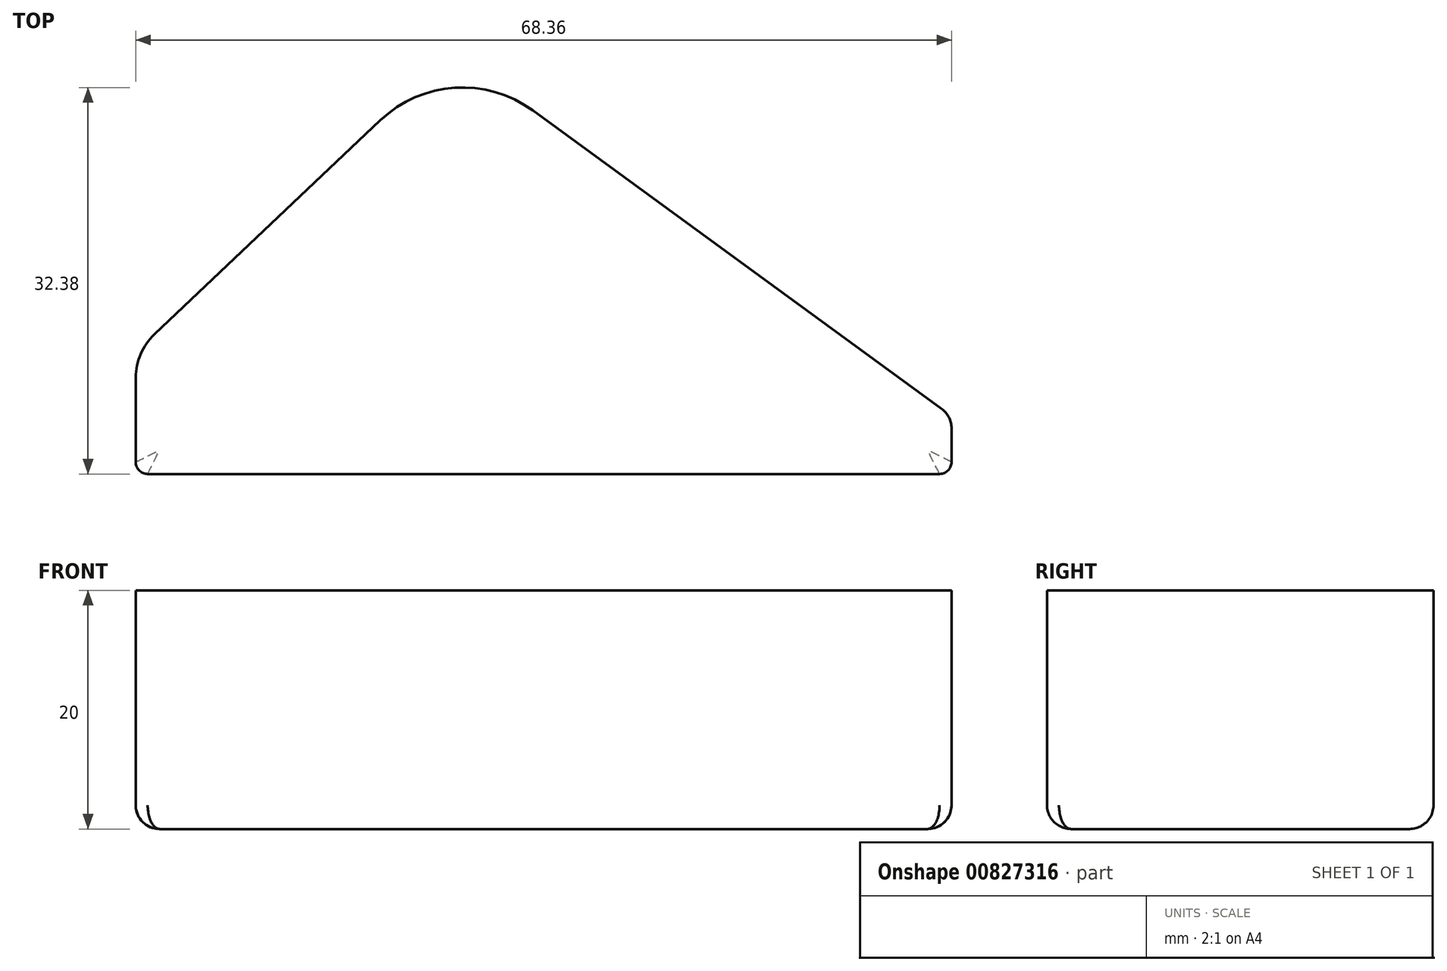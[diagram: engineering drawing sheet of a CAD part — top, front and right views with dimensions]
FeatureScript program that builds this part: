
annotation { "Feature Type Name" : "Feature", "Feature Type Description" : "" }
export const myFeature = defineFeature(function(context is Context, id is Id, definition is map)
    precondition{}
    {
        {
            var Q0;
            Q0=qCreatedBy(makeId("Top.planeOp"),FACE);
            var sketch = newSketch(context, id + "F0", { "sketchPlane" : qUnion([Q0])});
            skLineSegment(sketch, "E0", {"start": v(-34, 25) * mm, "end": v(-8.46, 25) * mm});
            skLineSegment(sketch, "E1", {"start": v(32.36, 25) * mm, "end": v(-8.46, 25) * mm});
            skLineSegment(sketch, "E2", {"start": v(-8.46, 25) * mm, "end": v(-8.46, 60.37) * mm});
            skLineSegment(sketch, "E3", {"start": v(-35, 26) * mm, "end": v(-35, 33.07) * mm});
            skLineSegment(sketch, "E4", {"start": v(-33.44, 36.7) * mm, "end": v(-14.5, 54.64) * mm});
            skLineSegment(sketch, "E5", {"start": v(-1.73, 55.46) * mm, "end": v(32.54, 30.45) * mm});
            skPoint(sketch, "E6.visualSharp", {"position": v(-35, 35.22) * mm});
            skArc(sketch, "E6.filletArc", {"start": v(-33.44, 36.7) * mm, "mid": v(-34.6, 35.04) * mm, "end": v(-35, 33.07) * mm});
            skPoint(sketch, "E7.visualSharp", {"position": v(-8.46, 60.37) * mm});
            skArc(sketch, "E7.filletArc", {"start": v(-1.73, 55.46) * mm, "mid": v(-8.27, 57.36) * mm, "end": v(-14.5, 54.64) * mm});
            skArc(sketch, "E8.filletArc", {"start": v(-35, 26) * mm, "mid": v(-34.7, 25.3) * mm, "end": v(-34, 25) * mm});
            skLineSegment(sketch, "E9", {"start": v(33.36, 26) * mm, "end": v(33.36, 28.83) * mm});
            skArc(sketch, "E10.filletArc", {"start": v(32.36, 25) * mm, "mid": v(33.07, 25.3) * mm, "end": v(33.36, 26) * mm});
            skPoint(sketch, "E11.visualSharp", {"position": v(33.36, 29.85) * mm});
            skArc(sketch, "E11.filletArc", {"start": v(33.36, 28.83) * mm, "mid": v(33.14, 29.74) * mm, "end": v(32.54, 30.45) * mm});
            skSolve(sketch);
        }
        {
            var Q0;
            {var subQ2=sQuery(id+"F0.wireOp",EDGE,"E0");Q0=makeQuery(id+"F0.imprint","IMPRINT",FACE,{"disambiguationData":[TD([[makeQuery(id+"F0.imprint","IMPRINT",EDGE,{"derivedFrom":subQ2}),1.0]])]});}
            var Q1;
            {var subQ1=sQuery(id+"F0.wireOp",EDGE,"E1");Q1=makeQuery(id+"F0.imprint","IMPRINT",FACE,{"disambiguationData":[TD([[makeQuery(id+"F0.imprint","IMPRINT",EDGE,{"derivedFrom":subQ1}),-1.0]])]});}
            extrude(context, id + "F1", {"entities" : qUnion([Q0, Q1]), "oppositeDirection" : true, "depth" : 20 * mm, "offsetDistance" : 25 * mm});
        }
        {
            var Q0;
            Q0=makeQuery(id+"F1.opExtrude","CAP_EDGE",EDGE,{"disambiguationData":[OSD([sQuery(id+"F0.wireOp",EDGE,"E0"),sQuery(id+"F0.wireOp",EDGE,"E1")])],"isStart":false});
            fillet(context, id + "F2", {"entities" : qUnion([Q0]), "radius" : 2 * mm, "tangentPropagation" : true, "allowEdgeOverflow" : false});
        }
    });
